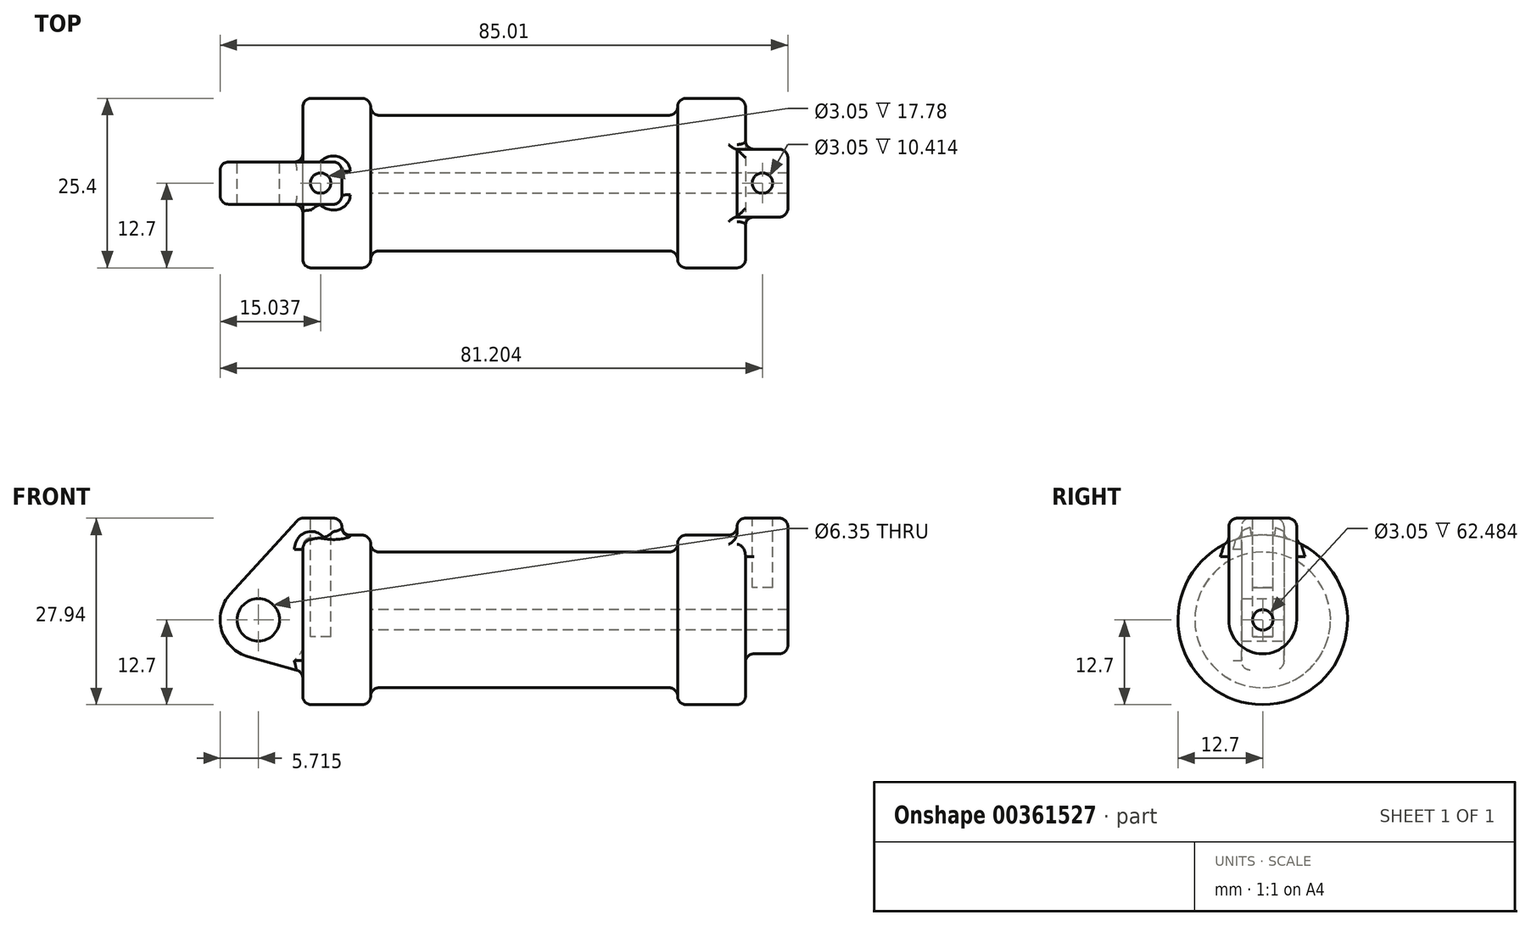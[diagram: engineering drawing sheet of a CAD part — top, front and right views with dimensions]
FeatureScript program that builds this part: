
annotation { "Feature Type Name" : "Feature", "Feature Type Description" : "" }
export const myFeature = defineFeature(function(context is Context, id is Id, definition is map)
    precondition{}
    {
        {
            var Q0;
            Q0=qCreatedBy(makeId("Front.planeOp"),FACE);
            var sketch = newSketch(context, id + "F0", { "sketchPlane" : qUnion([Q0])});
            skLineSegment(sketch, "E0", {"start": v(0, 0) * mm, "end": v(0, 12.7) * mm});
            skLineSegment(sketch, "E1", {"start": v(0, 12.7) * mm, "end": v(10.16, 12.7) * mm});
            skLineSegment(sketch, "E2", {"start": v(10.16, 12.7) * mm, "end": v(10.16, 10.16) * mm});
            skLineSegment(sketch, "E3", {"start": v(10.16, 10.16) * mm, "end": v(56.13, 10.16) * mm});
            skLineSegment(sketch, "E4", {"start": v(56.13, 10.16) * mm, "end": v(56.13, 12.7) * mm});
            skLineSegment(sketch, "E5", {"start": v(56.13, 12.7) * mm, "end": v(66.3, 12.7) * mm});
            skLineSegment(sketch, "E6", {"start": v(66.3, 12.7) * mm, "end": v(66.3, 0) * mm});
            skLineSegment(sketch, "E7", {"start": v(66.3, 0) * mm, "end": v(0, 0) * mm});
            skLineSegment(sketch, "E8", {"start": v(5.84, 15.24) * mm, "end": v(-0.5, 15.24) * mm});
            skLineSegment(sketch, "E9", {"start": v(-0.5, 15.24) * mm, "end": v(-10.88, 3.85) * mm});
            skLineSegment(sketch, "E10", {"start": v(0, 0) * mm, "end": v(-6.65, 0) * mm});
            skCircle(sketch, "E11", {"center": v(-6.65, 0) * mm, "radius": 5.72 * mm});
            skCircle(sketch, "E12", {"center": v(-6.65, 0) * mm, "radius": 3.18 * mm});
            skLineSegment(sketch, "E13", {"start": v(5.84, 15.24) * mm, "end": v(5.84, -9.4) * mm});
            skLineSegment(sketch, "E14", {"start": v(5.84, -9.4) * mm, "end": v(-8.18, -5.5) * mm});
            skSolve(sketch);
        }
        {
            var Q0;
            {var subQ0=sQuery(id+"F0.wireOp",EDGE,"E2");Q0=makeQuery(id+"F0.imprint","IMPRINT",FACE,{"disambiguationData":[TD([[makeQuery(id+"F0.imprint","IMPRINT",EDGE,{"derivedFrom":subQ0}),-1.0]])]});}
            var Q1;
            {var subQ0=sQuery(id+"F0.wireOp",EDGE,"E0");Q1=makeQuery(id+"F0.imprint","IMPRINT",FACE,{"disambiguationData":[TD([[makeQuery(id+"F0.imprint","IMPRINT",EDGE,{"derivedFrom":subQ0}),-1.0]])]});}
            var Q2;
            Q2=sQuery(id+"F0.wireOp",EDGE,"E7");
            revolve(context, id + "F1", {"entities" : qUnion([Q0, Q1]), "axis" : qUnion([Q2]), "revolveType" : RevolveType.FULL});
        }
        {
            var Q0;
            {var subQ0=sQuery(id+"F0.wireOp",EDGE,"E0");Q0=makeQuery(id+"F0.imprint","IMPRINT",FACE,{"disambiguationData":[TD([[makeQuery(id+"F0.imprint","IMPRINT",EDGE,{"derivedFrom":subQ0}),-1.0]])]});}
            var Q1;
            {var subQ1=sQuery(id+"F0.wireOp",EDGE,"E0");Q1=makeQuery(id+"F0.imprint","IMPRINT",FACE,{"disambiguationData":[TD([[makeQuery(id+"F0.imprint","IMPRINT",EDGE,{"derivedFrom":subQ1}),1.0]])]});}
            var Q2;
            {var subQ5=sQuery(id+"F0.wireOp",EDGE,"E12");Q2=makeQuery(id+"F0.imprint","IMPRINT",FACE,{"disambiguationData":[TD([[makeQuery(id+"F0.imprint","IMPRINT",EDGE,{"derivedFrom":subQ5}),-1.0]])]});}
            var Q3;
            {var subQ0=sQuery(id+"F0.wireOp",EDGE,"E14");Q3=makeQuery(id+"F0.imprint","IMPRINT",FACE,{"disambiguationData":[TD([[makeQuery(id+"F0.imprint","IMPRINT",EDGE,{"derivedFrom":subQ0}),-1.0]])]});}
            extrude(context, id + "F2", {"entities" : qUnion([Q0, Q1, Q2, Q3]), "operationType" : NewBodyOperationType.ADD, "endBound" : BoundingType.SYMMETRIC, "depth" : 6.35 * mm});
        }
        {
            var Q0;
            Q0=makeQuery(id+"F1.opRevolve","SWEPT_FACE",FACE,{"disambiguationData":[OSD([sQuery(id+"F0.wireOp",EDGE,"E6")])]});
            var sketch = newSketch(context, id + "F3", { "sketchPlane" : qUnion([Q0])});
            skCircle(sketch, "E15", {"center": v(0, 0) * mm, "radius": 5.08 * mm});
            skLineSegment(sketch, "E16", {"start": v(-5.08, 15.24) * mm, "end": v(-5.08, 0) * mm});
            skLineSegment(sketch, "E17", {"start": v(5.08, 15.24) * mm, "end": v(5.08, 0) * mm});
            skCircle(sketch, "E18", {"center": v(0, 0) * mm, "radius": 1.52 * mm});
            skLineSegment(sketch, "E19", {"start": v(-5.08, 15.24) * mm, "end": v(5.08, 15.24) * mm});
            skSolve(sketch);
        }
        {
            var Q0;
            Q0 = qSketchRegion(id + "F3", true);
            extrude(context, id + "F4", {"entities" : qUnion([Q0]), "operationType" : NewBodyOperationType.ADD, "depth" : 6.35 * mm, "hasSecondDirection" : true, "secondDirectionOppositeDirection" : true, "secondDirectionDepth" : 1.27 * mm});
        }
        {
            var Q0;
            Q0=makeQuery(id+"F2.opExtrude","SWEPT_FACE",FACE,{"disambiguationData":[OSD([sQuery(id+"F0.wireOp",EDGE,"E8")])]});
            var sketch = newSketch(context, id + "F5", { "sketchPlane" : qUnion([Q0])});
            skCircle(sketch, "E20", {"center": v(2.67, 0) * mm, "radius": 1.52 * mm});
            skPoint(sketch, "E20.centerSnap0", {"position": v(2.67, 3.18) * mm});
            skPoint(sketch, "E20.centerSnap1", {"position": v(5.84, 0) * mm});
            skSolve(sketch);
        }
        {
            var Q0;
            Q0=makeQuery(id+"F5.imprint","IMPRINT",FACE,{"disambiguationData":[TD([[makeQuery(id+"F5.imprint","IMPRINT",EDGE,{"derivedFrom":sQuery(id+"F5.wireOp",EDGE,"E20")}),1.0]])]});
            var Q1;
            Q1=sQuery(id+"F5.wireOp",EDGE,"E20");
            extrude(context, id + "F6", {"entities" : qUnion([Q0]), "operationType" : NewBodyOperationType.REMOVE, "surfaceEntities" : qUnion([Q1]), "oppositeDirection" : true, "depth" : 17.78 * mm});
        }
        {
            var Q0;
            Q0=makeQuery(id+"F4.opExtrude","SWEPT_FACE",FACE,{"disambiguationData":[OSD([sQuery(id+"F3.wireOp",EDGE,"E19")])]});
            var sketch = newSketch(context, id + "F7", { "sketchPlane" : qUnion([Q0])});
            skLineSegment(sketch, "E21", {"start": v(68.83, -5.08) * mm, "end": v(68.83, 5.08) * mm, "construction": true});
            skCircle(sketch, "E22", {"center": v(68.83, 0) * mm, "radius": 1.52 * mm});
            skSolve(sketch);
        }
        {
            var Q0;
            Q0=makeQuery(id+"F7.imprint","IMPRINT",FACE,{"disambiguationData":[TD([[makeQuery(id+"F7.imprint","IMPRINT",EDGE,{"derivedFrom":sQuery(id+"F7.wireOp",EDGE,"E22")}),1.0]])]});
            extrude(context, id + "F8", {"entities" : qUnion([Q0]), "operationType" : NewBodyOperationType.REMOVE, "oppositeDirection" : true, "depth" : 10.4 * mm});
        }
        {
            var Q0;
            Q0=makeQuery(id+"F1.opRevolve","SWEPT_EDGE",EDGE,{"disambiguationData":[OSD([sQuery(id+"F0.wireOp",EDGE,"E0"),sQuery(id+"F0.wireOp",EDGE,"E1")])]});
            var Q1;
            Q1=makeQuery(id+"F2.boolean.opBoolean","INTERSECT",EDGE,{"derivedFrom":[makeQuery(id+"F1.opRevolve","SWEPT_FACE",FACE,{"disambiguationData":[OSD([sQuery(id+"F0.wireOp",EDGE,"E0")])]}),makeQuery(id+"F2.opExtrude","CAP_FACE",FACE,{"disambiguationData":[OSD([sQuery(id+"F0.wireOp",EDGE,"E8"),sQuery(id+"F0.wireOp",EDGE,"E9"),sQuery(id+"F0.wireOp",EDGE,"E11"),sQuery(id+"F0.wireOp",EDGE,"E12"),sQuery(id+"F0.wireOp",EDGE,"E13"),sQuery(id+"F0.wireOp",EDGE,"E14")])],"isStart":false})]});
            var Q2;
            Q2=makeQuery(id+"F2.boolean.opBoolean","INTERSECT",EDGE,{"derivedFrom":[makeQuery(id+"F1.opRevolve","SWEPT_FACE",FACE,{"disambiguationData":[OSD([sQuery(id+"F0.wireOp",EDGE,"E0")])]}),makeQuery(id+"F2.opExtrude","SWEPT_FACE",FACE,{"disambiguationData":[OSD([sQuery(id+"F0.wireOp",EDGE,"E14")])]})]});
            var Q3;
            Q3=makeQuery(id+"F2.opExtrude","CAP_EDGE",EDGE,{"disambiguationData":[OSD([sQuery(id+"F0.wireOp",EDGE,"E14")])],"isStart":false});
            var Q4;
            Q4=makeQuery(id+"F2.opExtrude","SWEPT_EDGE",EDGE,{"disambiguationData":[OSD([sQuery(id+"F0.wireOp",EDGE,"E11"),sQuery(id+"F0.wireOp",EDGE,"E14")])]});
            var Q5;
            Q5=makeQuery(id+"F2.opExtrude","SWEPT_EDGE",EDGE,{"disambiguationData":[OSD([sQuery(id+"F0.wireOp",EDGE,"E9"),sQuery(id+"F0.wireOp",EDGE,"E11")])]});
            var Q6;
            Q6=makeQuery(id+"F2.opExtrude","CAP_EDGE",EDGE,{"disambiguationData":[OSD([sQuery(id+"F0.wireOp",EDGE,"E11")])],"isStart":true});
            var Q7;
            Q7=makeQuery(id+"F2.opExtrude","CAP_EDGE",EDGE,{"disambiguationData":[OSD([sQuery(id+"F0.wireOp",EDGE,"E8")])],"isStart":true});
            var Q8;
            Q8=makeQuery(id+"F2.opExtrude","SWEPT_EDGE",EDGE,{"disambiguationData":[OSD([sQuery(id+"F0.wireOp",EDGE,"E8"),sQuery(id+"F0.wireOp",EDGE,"E9")])]});
            var Q9;
            Q9=makeQuery(id+"F2.opExtrude","CAP_EDGE",EDGE,{"disambiguationData":[OSD([sQuery(id+"F0.wireOp",EDGE,"E8")])],"isStart":false});
            var Q10;
            Q10=makeQuery(id+"F2.opExtrude","CAP_EDGE",EDGE,{"disambiguationData":[OSD([sQuery(id+"F0.wireOp",EDGE,"E13")])],"isStart":false});
            var Q11;
            Q11=makeQuery(id+"F2.opExtrude","SWEPT_FACE",FACE,{"disambiguationData":[OSD([sQuery(id+"F0.wireOp",EDGE,"E13")])]});
            fillet(context, id + "F9", {"entities" : qUnion([Q0, Q1, Q2, Q3, Q4, Q5, Q6, Q7, Q8, Q9, Q10, Q11]), "radius" : 1.27 * mm, "tangentPropagation" : true, "allowEdgeOverflow" : false});
        }
        {
            var Q0;
            Q0=makeQuery(id+"F3.imprint","IMPRINT",FACE,{"disambiguationData":[TD([[makeQuery(id+"F3.imprint","IMPRINT",EDGE,{"derivedFrom":sQuery(id+"F3.wireOp",EDGE,"E18")}),1.0]])]});
            var Q1;
            Q1=makeQuery(id+"F1.opRevolve","SWEPT_FACE",FACE,{"disambiguationData":[OSD([sQuery(id+"F0.wireOp",EDGE,"E2")])]});
            extrude(context, id + "F10", {"entities" : qUnion([Q0]), "operationType" : NewBodyOperationType.REMOVE, "endBound" : BoundingType.UP_TO_SURFACE, "oppositeDirection" : true, "endBoundEntityFace" : qUnion([Q1]), "depth" : 25.4 * mm});
        }
        {
            var Q0;
            Q0=makeQuery(id+"F1.opRevolve","SWEPT_EDGE",EDGE,{"disambiguationData":[OSD([sQuery(id+"F0.wireOp",EDGE,"E2"),sQuery(id+"F0.wireOp",EDGE,"E3")])]});
            var Q1;
            Q1=makeQuery(id+"F1.opRevolve","SWEPT_EDGE",EDGE,{"disambiguationData":[OSD([sQuery(id+"F0.wireOp",EDGE,"E1"),sQuery(id+"F0.wireOp",EDGE,"E2")])]});
            var Q2;
            Q2=makeQuery(id+"F1.opRevolve","SWEPT_EDGE",EDGE,{"disambiguationData":[OSD([sQuery(id+"F0.wireOp",EDGE,"E3"),sQuery(id+"F0.wireOp",EDGE,"E4")])]});
            var Q3;
            Q3=makeQuery(id+"F1.opRevolve","SWEPT_EDGE",EDGE,{"disambiguationData":[OSD([sQuery(id+"F0.wireOp",EDGE,"E4"),sQuery(id+"F0.wireOp",EDGE,"E5")])]});
            var Q4;
            Q4=makeQuery(id+"F1.opRevolve","SWEPT_EDGE",EDGE,{"disambiguationData":[OSD([sQuery(id+"F0.wireOp",EDGE,"E5"),sQuery(id+"F0.wireOp",EDGE,"E6")])]});
            fillet(context, id + "F11", {"entities" : qUnion([Q0, Q1, Q2, Q3, Q4]), "radius" : 1.27 * mm, "tangentPropagation" : true, "allowEdgeOverflow" : false});
        }
        {
            var Q0;
            Q0=makeQuery(id+"F4.boolean.opBoolean","INTERSECT",EDGE,{"derivedFrom":[makeQuery(id+"F1.opRevolve","SWEPT_FACE",FACE,{"disambiguationData":[OSD([sQuery(id+"F0.wireOp",EDGE,"E5")])]}),makeQuery(id+"F4.opExtrude","CAP_FACE",FACE,{"disambiguationData":[OSD([sQuery(id+"F3.wireOp",EDGE,"E15"),sQuery(id+"F3.wireOp",EDGE,"E16"),sQuery(id+"F3.wireOp",EDGE,"E17"),sQuery(id+"F3.wireOp",EDGE,"E18"),sQuery(id+"F3.wireOp",EDGE,"E19")])],"isStart":true})]});
            var Q1;
            Q1=makeQuery(id+"F4.opExtrude","CAP_EDGE",EDGE,{"disambiguationData":[OSD([sQuery(id+"F3.wireOp",EDGE,"E19")])],"isStart":true});
            var Q2;
            Q2=makeQuery(id+"F4.opExtrude","SWEPT_EDGE",EDGE,{"disambiguationData":[OSD([sQuery(id+"F3.wireOp",EDGE,"E16"),sQuery(id+"F3.wireOp",EDGE,"E19")])]});
            var Q3;
            Q3=makeQuery(id+"F4.opExtrude","CAP_EDGE",EDGE,{"disambiguationData":[OSD([sQuery(id+"F3.wireOp",EDGE,"E19")])],"isStart":false});
            var Q4;
            Q4=makeQuery(id+"F4.opExtrude","SWEPT_EDGE",EDGE,{"disambiguationData":[OSD([sQuery(id+"F3.wireOp",EDGE,"E17"),sQuery(id+"F3.wireOp",EDGE,"E19")])]});
            var Q5;
            Q5=makeQuery(id+"F4.opExtrude","CAP_EDGE",EDGE,{"disambiguationData":[OSD([sQuery(id+"F3.wireOp",EDGE,"E16")])],"isStart":false});
            var Q6;
            Q6=makeQuery(id+"F4.boolean.opBoolean","INTERSECT",EDGE,{"derivedFrom":[makeQuery(id+"F1.opRevolve","SWEPT_FACE",FACE,{"disambiguationData":[OSD([sQuery(id+"F0.wireOp",EDGE,"E6")])]}),makeQuery(id+"F4.opExtrude","SWEPT_FACE",FACE,{"disambiguationData":[OSD([sQuery(id+"F3.wireOp",EDGE,"E16")])]})]});
            fillet(context, id + "F12", {"entities" : qUnion([Q0, Q1, Q2, Q3, Q4, Q5, Q6]), "radius" : 1.27 * mm, "tangentPropagation" : true, "allowEdgeOverflow" : false});
        }
    });
